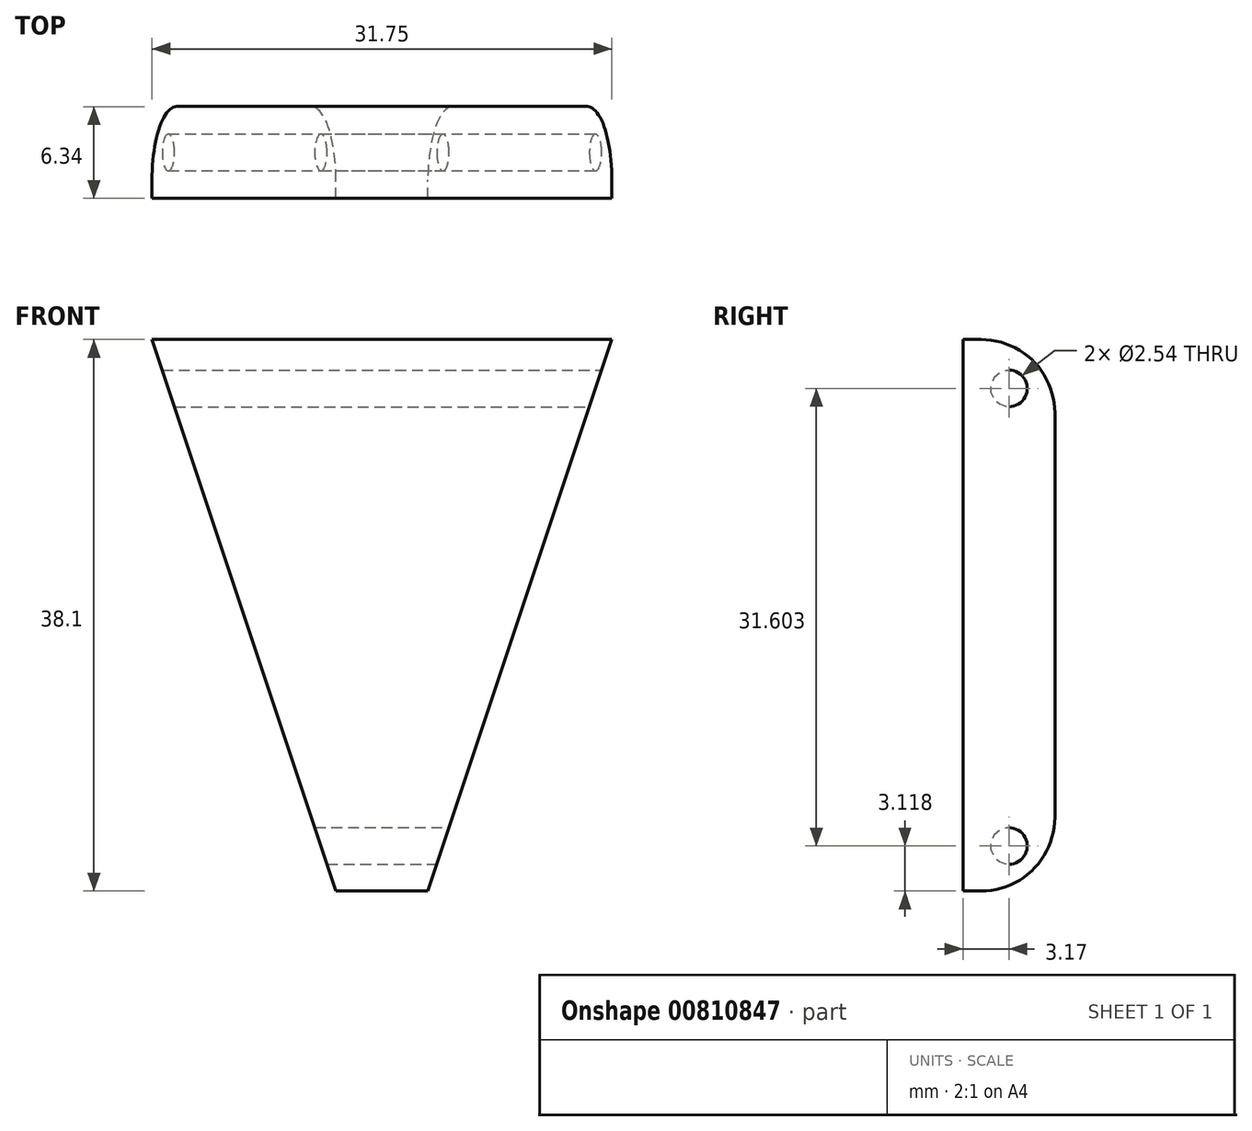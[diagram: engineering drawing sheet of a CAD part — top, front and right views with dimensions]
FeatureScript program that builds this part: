
annotation { "Feature Type Name" : "Feature", "Feature Type Description" : "" }
export const myFeature = defineFeature(function(context is Context, id is Id, definition is map)
    precondition{}
    {
        {
            var Q0;
            Q0=qCreatedBy(makeId("Front.planeOp"),FACE);
            var sketch = newSketch(context, id + "F0", { "sketchPlane" : qUnion([Q0])});
            skLineSegment(sketch, "E0", {"start": v(-15.9, 17.01) * mm, "end": v(15.85, 17.01) * mm});
            skLineSegment(sketch, "E1", {"start": v(3.15, -21.09) * mm, "end": v(-3.2, -21.09) * mm});
            skLineSegment(sketch, "E2", {"start": v(-15.9, 17.01) * mm, "end": v(-3.2, -21.09) * mm});
            skLineSegment(sketch, "E3", {"start": v(3.15, -21.09) * mm, "end": v(15.85, 17.01) * mm});
            skLineSegment(sketch, "E4", {"start": v(15.85, 17.01) * mm, "end": v(15.85, -21.09) * mm, "construction": true});
            skLineSegment(sketch, "E5", {"start": v(15.85, -21.09) * mm, "end": v(3.15, -21.09) * mm, "construction": true});
            skLineSegment(sketch, "E6", {"start": v(-15.9, 17.01) * mm, "end": v(-15.9, -21.09) * mm, "construction": true});
            skLineSegment(sketch, "E7", {"start": v(-15.9, -21.09) * mm, "end": v(-3.2, -21.09) * mm, "construction": true});
            skSolve(sketch);
        }
        {
            var Q0;
            Q0 = qSketchRegion(id + "F0", true);
            extrude(context, id + "F1", {"entities" : qUnion([Q0]), "endBound" : BoundingType.SYMMETRIC, "depth" : 6.35 * mm, "offsetDistance" : 25.4 * mm});
        }
        {
            var Q0;
            Q0=makeQuery(id+"F1.opExtrude","CAP_EDGE",EDGE,{"disambiguationData":[OSD([sQuery(id+"F0.wireOp",EDGE,"E0")])],"isStart":true});
            var Q1;
            Q1=makeQuery(id+"F1.opExtrude","CAP_EDGE",EDGE,{"disambiguationData":[OSD([sQuery(id+"F0.wireOp",EDGE,"E1")])],"isStart":true});
            fillet(context, id + "F2", {"entities" : qUnion([Q0, Q1]), "radius" : 5.08 * mm, "tangentPropagation" : true, "allowEdgeOverflow" : false});
        }
        {
            var Q0;
            Q0=qCreatedBy(makeId("Right.planeOp"),FACE);
            var sketch = newSketch(context, id + "F3", { "sketchPlane" : qUnion([Q0])});
            skCircle(sketch, "E8", {"center": v(0, 13.63) * mm, "radius": 1.27 * mm});
            skCircle(sketch, "E9", {"center": v(0, -17.97) * mm, "radius": 1.27 * mm});
            skSolve(sketch);
        }
        {
            var Q0;
            Q0 = qSketchRegion(id + "F3", true);
            extrude(context, id + "F4", {"entities" : qUnion([Q0]), "operationType" : NewBodyOperationType.REMOVE, "endBound" : BoundingType.SYMMETRIC, "oppositeDirection" : true, "depth" : 50.8 * mm, "offsetDistance" : 25.4 * mm});
        }
    });
